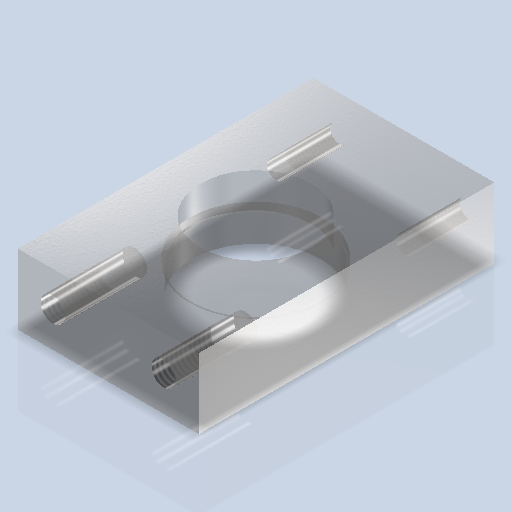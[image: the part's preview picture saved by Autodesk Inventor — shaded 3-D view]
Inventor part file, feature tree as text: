
AUTODESK INVENTOR PART (.ipt)
format: ipt  version: 2024 (Build 280153000, 153)  size: 254,464 bytes
history: native  units: mm
features: other x3, sketch x3, plane x1
ambient origin geometry x8: Origin, YZ Plane, XZ Plane, XY Plane, X Axis, Y Axis, Z Axis, Center Point
bodies: Volumenkörper1 (feature_tree)
feature tree (7):
  other  "Lagerbock.ipt"
  other  "Volumenkörper1::Lagerbock.ipt"
  other  "Bezeichnung1"
  sketch  "Skizze1"  dims[d0=10.0mm]
  sketch  "Skizze2"
  sketch  "Skizze3"
  plane  "Arbeitsebene1"
